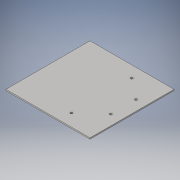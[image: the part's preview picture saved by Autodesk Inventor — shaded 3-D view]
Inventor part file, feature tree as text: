
AUTODESK INVENTOR PART (.ipt)
format: ipt  version: 2016 (Build 200138000, 138)  size: 105,472 bytes
history: native  units: in
note: dims shown in document units (in); Inventor stores cm internally (conversion verified against a paired STEP export)
features: sketch x2, extrude x1, hole x1
ambient origin geometry x8: Origin, YZ Plane, XZ Plane, XY Plane, X Axis, Y Axis, Z Axis, Center Point
bodies: Solid1 (feature_tree)
feature tree (4):
  extrude  "Extrusion1"  Depth=8.5in
  hole  "Hole1"  [1 undecoded]
  sketch  "Sketch1"  dims[d0=8.5in d1=8.5in]
  sketch  "Sketch2"  dims[d2=0.125in d3=0.0in d4=5.4331in d5=1.0236in d6=3.1102in d7=0.9843in d8=3.1102in d9=1.0236in d10=2.874in d11=7.0866in d12=0.25in d13=0.0in d14=0.2362in d15=0.75in d16=0.375in d17=0.25in d18=0.5635in d19=1.0in d20=0.8108in]
note: 1 required parameter value undecoded (feature->parameter linkage not recoverable at this tier; creation-order binding heuristic only, values carry confidence <= 0.55)
